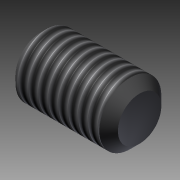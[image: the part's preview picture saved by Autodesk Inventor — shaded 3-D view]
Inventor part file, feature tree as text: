
AUTODESK INVENTOR PART (.ipt)
format: ipt  version: 2016 (Build 200138000, 138)  size: 129,536 bytes
history: native  units: mm
features: other x7, sketch x3, revolve x2, thread x1, extrude x1
ambient origin geometry x8: Origin, YZ Plane, XZ Plane, XY Plane, X Axis, Y Axis, Z Axis, Center Point
bodies: Solid1 (feature_tree)
feature tree (14):
  revolve  "Revolution1"  [1 undecoded]
  thread  "Thread1"  [1 undecoded]
  extrude  "Extrusion1"  TaperAngle=0.0deg  [1 undecoded]
  revolve  "Revolution2"  [1 undecoded]
  other  "CP_XY"
  other  "CP_YZ"
  other  "CP_ZX"
  other  "CP_X"
  other  "CP_Y"
  other  "CP_Z"
  other  "CP_Center"
  sketch  "Sketch_1"  dims[d0=360.0deg d1=6.7595mm d2=0.0mm d3=2.0mm d4=0.0mm]
  sketch  "Sketch_2"  dims[d5=360.0deg d6=0.0mm]
  sketch  "Sketch_3"
note: 4 required parameter values undecoded (feature->parameter linkage not recoverable at this tier; creation-order binding heuristic only, values carry confidence <= 0.55)